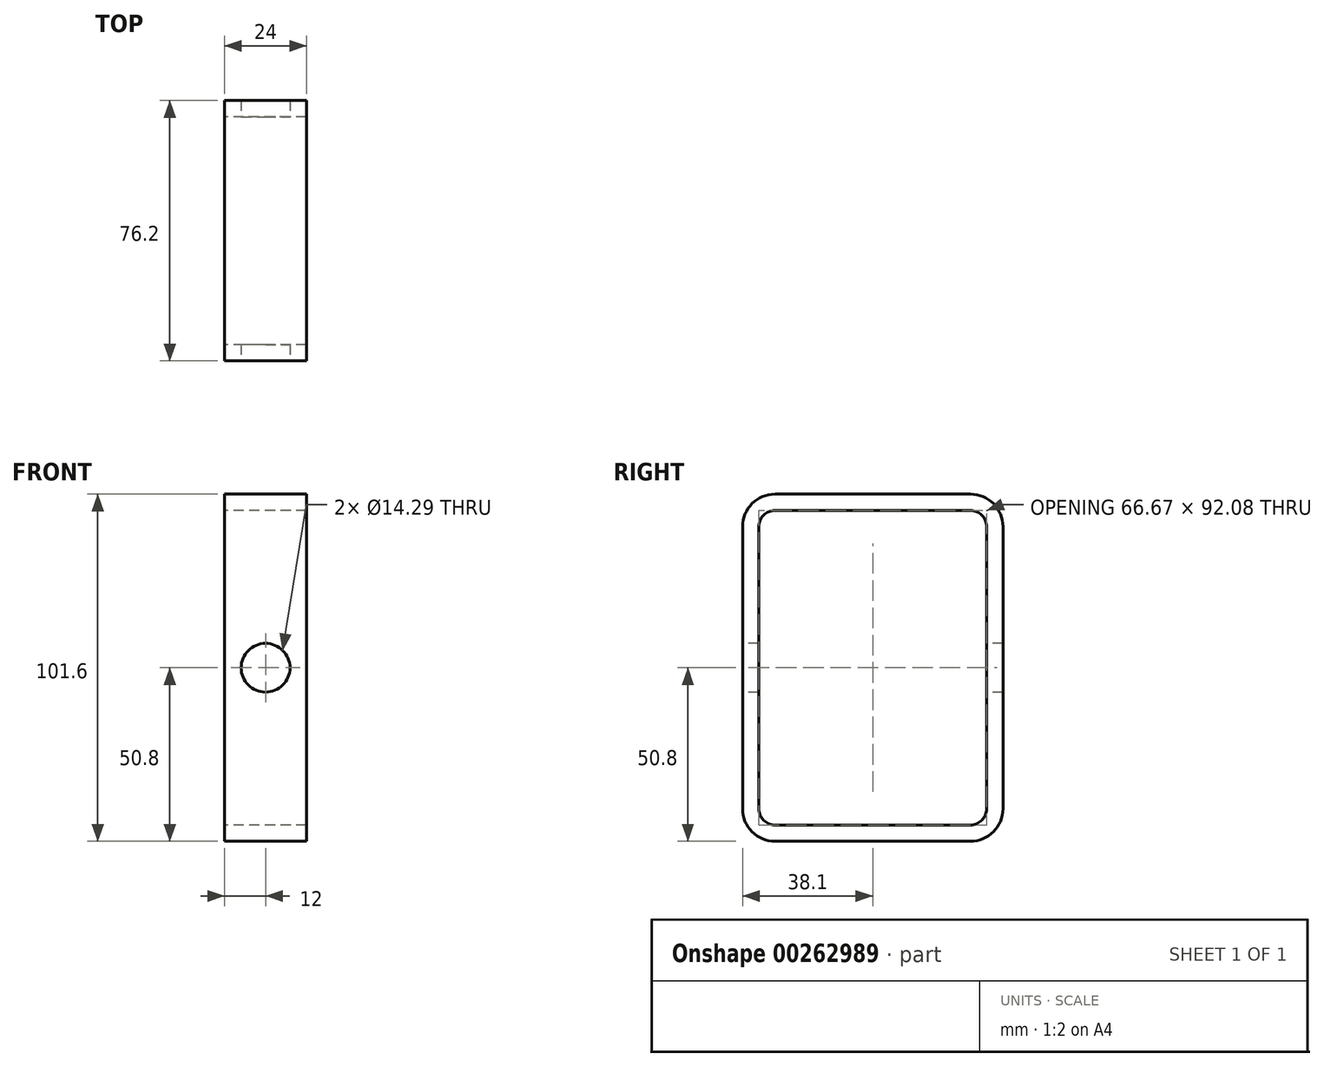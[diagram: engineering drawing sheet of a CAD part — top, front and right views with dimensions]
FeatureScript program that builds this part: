
annotation { "Feature Type Name" : "Feature", "Feature Type Description" : "" }
export const myFeature = defineFeature(function(context is Context, id is Id, definition is map)
    precondition{}
    {
        {
            assignVariable(context, id + "F0", {"name" : "Length", "anyValue" : 24});
        }
        {
            var Q0;
            Q0=qCreatedBy(makeId("Right.planeOp"),FACE);
            var sketch = newSketch(context, id + "F1", { "sketchPlane" : qUnion([Q0])});
            skLineSegment(sketch, "E0.bottom", {"start": v(-28.58, 50.8) * mm, "end": v(28.58, 50.8) * mm});
            skLineSegment(sketch, "E0.top", {"start": v(-28.58, -50.8) * mm, "end": v(28.58, -50.8) * mm});
            skLineSegment(sketch, "E0.left", {"start": v(-38.1, 41.28) * mm, "end": v(-38.1, -41.28) * mm});
            skLineSegment(sketch, "E0.right", {"start": v(38.1, 41.28) * mm, "end": v(38.1, -41.28) * mm});
            skPoint(sketch, "E0.middle", {"position": v(0, 0) * mm});
            skPoint(sketch, "E1.visualSharp", {"position": v(-38.1, 50.8) * mm});
            skArc(sketch, "E1.filletArc", {"start": v(-28.58, 50.8) * mm, "mid": v(-35.31, 48.01) * mm, "end": v(-38.1, 41.28) * mm});
            skPoint(sketch, "E2.visualSharp", {"position": v(-33.34, 46.04) * mm});
            skPoint(sketch, "E3.visualSharp", {"position": v(38.1, 50.8) * mm});
            skArc(sketch, "E3.filletArc", {"start": v(38.1, 41.28) * mm, "mid": v(35.31, 48.01) * mm, "end": v(28.58, 50.8) * mm});
            skPoint(sketch, "E4.visualSharp", {"position": v(33.34, 46.04) * mm});
            skPoint(sketch, "E5.visualSharp", {"position": v(33.34, -46.04) * mm});
            skPoint(sketch, "E6.visualSharp", {"position": v(-33.34, -46.04) * mm});
            skPoint(sketch, "E7.visualSharp", {"position": v(38.1, -50.8) * mm});
            skArc(sketch, "E7.filletArc", {"start": v(28.58, -50.8) * mm, "mid": v(35.31, -48.01) * mm, "end": v(38.1, -41.28) * mm});
            skPoint(sketch, "E8.visualSharp", {"position": v(-38.1, -50.8) * mm});
            skArc(sketch, "E8.filletArc", {"start": v(-38.1, -41.28) * mm, "mid": v(-35.31, -48.01) * mm, "end": v(-28.58, -50.8) * mm});
            skLineSegment(sketch, "E9.0", {"start": v(-28.57, 46.04) * mm, "end": v(28.58, 46.04) * mm});
            skArc(sketch, "E9.1", {"start": v(33.34, 41.28) * mm, "mid": v(31.94, 44.64) * mm, "end": v(28.58, 46.04) * mm});
            skArc(sketch, "E9.2", {"start": v(-28.57, 46.04) * mm, "mid": v(-31.94, 44.64) * mm, "end": v(-33.34, 41.28) * mm});
            skLineSegment(sketch, "E9.3", {"start": v(33.34, 41.28) * mm, "end": v(33.34, -41.28) * mm});
            skLineSegment(sketch, "E9.4", {"start": v(-33.34, 41.28) * mm, "end": v(-33.34, -41.28) * mm});
            skArc(sketch, "E9.5", {"start": v(-33.34, -41.28) * mm, "mid": v(-31.94, -44.64) * mm, "end": v(-28.58, -46.04) * mm});
            skLineSegment(sketch, "E9.6", {"start": v(-28.58, -46.04) * mm, "end": v(28.57, -46.04) * mm});
            skArc(sketch, "E9.7", {"start": v(28.57, -46.04) * mm, "mid": v(31.94, -44.64) * mm, "end": v(33.34, -41.28) * mm});
            skSolve(sketch);
        }
        {
            var Q0;
            Q0=makeQuery(id+"F1.imprint","IMPRINT",FACE,{"disambiguationData":[TD([[makeQuery(id+"F1.imprint","IMPRINT",EDGE,{"derivedFrom":sQuery(id+"F1.wireOp",EDGE,"E0.bottom")}),-1.0]])]});
            var Q1;
            Q1=sQuery(id+"F1.wireOp",EDGE,"E1.filletArc");
            var Q2;
            Q2=sQuery(id+"F1.wireOp",EDGE,"E0.left");
            var Q3;
            Q3=sQuery(id+"F1.wireOp",EDGE,"E0.bottom");
            var Q4;
            Q4=sQuery(id+"F1.wireOp",EDGE,"E3.filletArc");
            var Q5;
            Q5=sQuery(id+"F1.wireOp",EDGE,"E0.right");
            var Q6;
            Q6=sQuery(id+"F1.wireOp",EDGE,"E7.filletArc");
            var Q7;
            Q7=sQuery(id+"F1.wireOp",EDGE,"E0.top");
            var Q8;
            Q8=sQuery(id+"F1.wireOp",EDGE,"E8.filletArc");
            extrude(context, id + "F2", {"entities" : qUnion([Q0]), "surfaceEntities" : qUnion([Q1, Q2, Q3, Q4, Q5, Q6, Q7, Q8]), "endBound" : BoundingType.SYMMETRIC, "depth" : (getVariable(context, 'Length')) * mm, "hasSecondDirection" : true, "secondDirectionOppositeDirection" : true, "secondDirectionDepth" : 25.4 * mm});
        }
        {
            var Q0;
            Q0=makeQuery(id+"F2.opExtrude","SWEPT_FACE",FACE,{"disambiguationData":[OSD([sQuery(id+"F1.wireOp",EDGE,"E0.left")])]});
            var sketch = newSketch(context, id + "F3", { "sketchPlane" : qUnion([Q0])});
            skPoint(sketch, "E10", {"position": v(-254, 0) * mm});
            skPoint(sketch, "E11", {"position": v(0, 0) * mm});
            skPoint(sketch, "E12", {"position": v(254, 0) * mm});
            skLineSegment(sketch, "E13", {"start": v(-254, 0) * mm, "end": v(0, 0) * mm, "construction": true});
            skLineSegment(sketch, "E14", {"start": v(0, 0) * mm, "end": v(254, 0) * mm, "construction": true});
            skSolve(sketch);
        }
        {
            var Q0;
            Q0=sQuery(id+"F3.wireOp",VERTEX,"E10");
            var Q1;
            Q1=sQuery(id+"F3.wireOp",VERTEX,"E11");
            var Q2;
            Q2=sQuery(id+"F3.wireOp",VERTEX,"E12");
            var Q3;
            Q3=makeQuery(id+"F2.opExtrude","SWEPT_BODY",BODY,{"disambiguationData":[OSD([sQuery(id+"F1.wireOp",EDGE,"E0.bottom"),sQuery(id+"F1.wireOp",EDGE,"E0.top"),sQuery(id+"F1.wireOp",EDGE,"E0.left"),sQuery(id+"F1.wireOp",EDGE,"E0.right"),sQuery(id+"F1.wireOp",EDGE,"E1.filletArc"),sQuery(id+"F1.wireOp",EDGE,"E3.filletArc"),sQuery(id+"F1.wireOp",EDGE,"E7.filletArc"),sQuery(id+"F1.wireOp",EDGE,"E8.filletArc"),sQuery(id+"F1.wireOp",EDGE,"E9.0"),sQuery(id+"F1.wireOp",EDGE,"E9.1"),sQuery(id+"F1.wireOp",EDGE,"E9.2"),sQuery(id+"F1.wireOp",EDGE,"E9.3"),sQuery(id+"F1.wireOp",EDGE,"E9.4"),sQuery(id+"F1.wireOp",EDGE,"E9.5"),sQuery(id+"F1.wireOp",EDGE,"E9.6"),sQuery(id+"F1.wireOp",EDGE,"E9.7")])]});
            hole(context, id + "F4", {"style" : HoleStyle.SIMPLE, "endStyle" : HoleEndStyle.THROUGH, "holeDiameter" : 14.29 * mm, "tappedDepth" : 12.7 * mm, "tapClearance" : 3, "locations" : qUnion([Q0, Q1, Q2]), "scope" : qUnion([Q3])});
        }
    });
